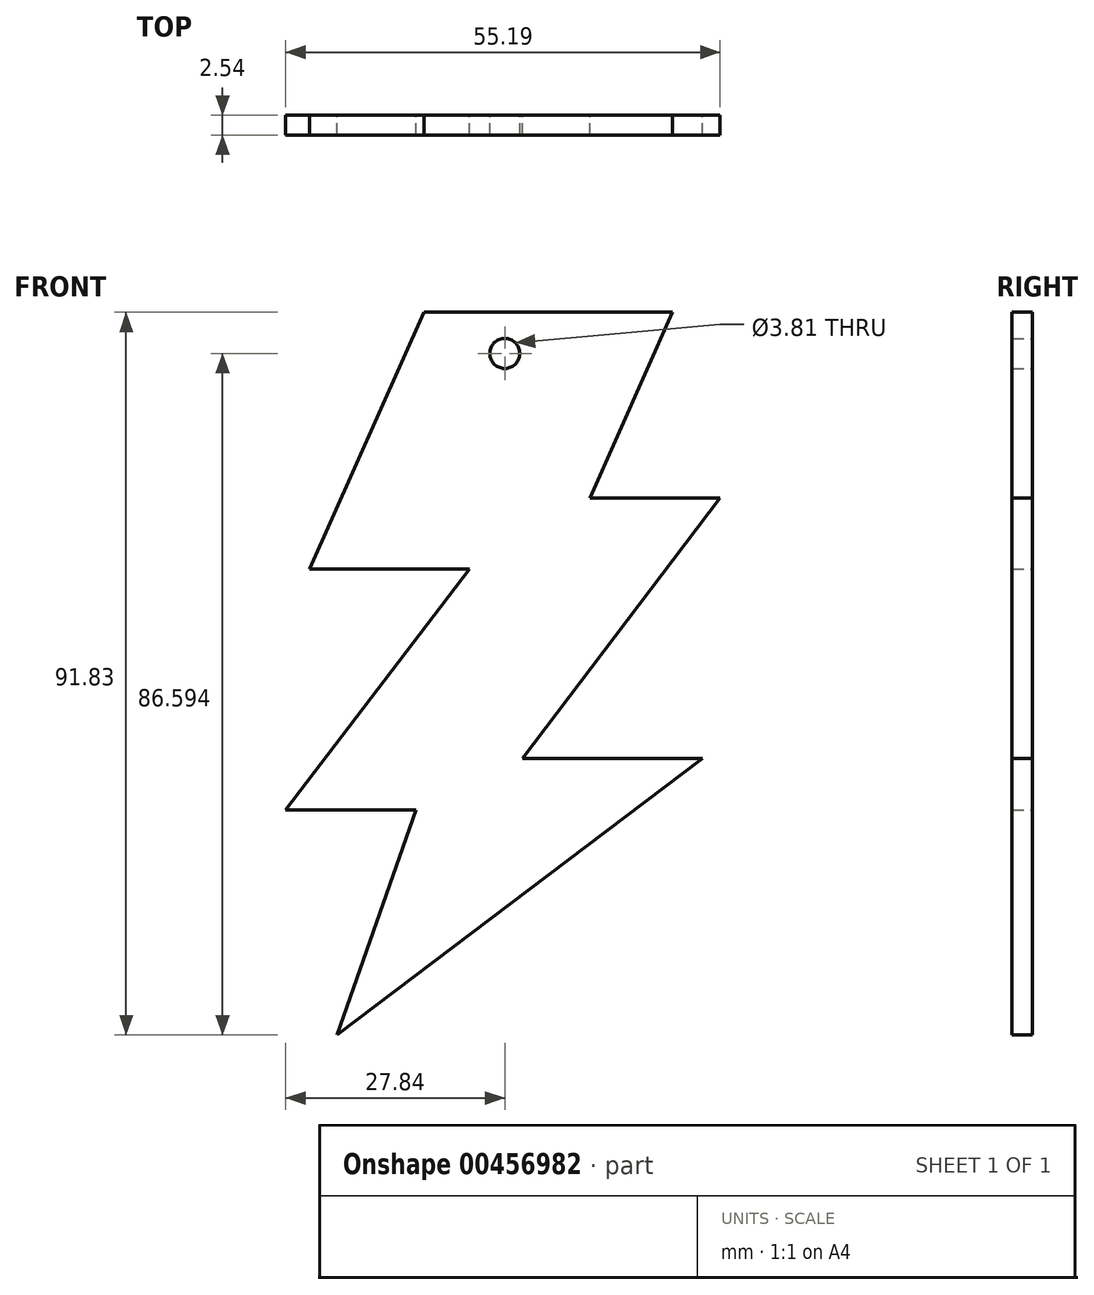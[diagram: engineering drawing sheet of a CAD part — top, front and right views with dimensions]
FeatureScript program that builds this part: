
annotation { "Feature Type Name" : "Feature", "Feature Type Description" : "" }
export const myFeature = defineFeature(function(context is Context, id is Id, definition is map)
    precondition{}
    {
        {
            var Q0;
            Q0=qCreatedBy(makeId("Front.planeOp"),FACE);
            var sketch = newSketch(context, id + "F0", { "sketchPlane" : qUnion([Q0])});
            skLineSegment(sketch, "E0", {"start": v(0, 76.78) * mm, "end": v(-31.6, 76.78) * mm});
            skLineSegment(sketch, "E1", {"start": v(-31.6, 76.78) * mm, "end": v(-46.16, 44.16) * mm});
            skLineSegment(sketch, "E2", {"start": v(-46.16, 44.16) * mm, "end": v(-25.84, 44.16) * mm});
            skLineSegment(sketch, "E3", {"start": v(-25.84, 44.16) * mm, "end": v(-49.17, 13.55) * mm});
            skLineSegment(sketch, "E4", {"start": v(-49.17, 13.55) * mm, "end": v(-32.62, 13.55) * mm});
            skLineSegment(sketch, "E5", {"start": v(0, 76.78) * mm, "end": v(-10.54, 53.19) * mm});
            skLineSegment(sketch, "E6", {"start": v(-10.54, 53.19) * mm, "end": v(6.02, 53.19) * mm});
            skLineSegment(sketch, "E7", {"start": v(6.02, 53.19) * mm, "end": v(-19.07, 20.07) * mm});
            skLineSegment(sketch, "E8", {"start": v(-19.07, 20.07) * mm, "end": v(3.76, 20.07) * mm});
            skLineSegment(sketch, "E9", {"start": v(3.76, 20.07) * mm, "end": v(-42.65, -15.05) * mm});
            skLineSegment(sketch, "E10", {"start": v(-42.65, -15.05) * mm, "end": v(-32.62, 13.55) * mm});
            skCircle(sketch, "E11", {"center": v(-21.33, 71.54) * mm, "radius": 1.9 * mm});
            skSolve(sketch);
        }
        {
            var Q0;
            Q0 = qSketchRegion(id + "F0", true);
            extrude(context, id + "F1", {"entities" : qUnion([Q0]), "depth" : 2.54 * mm});
        }
        {
            var Q0;
            Q0=makeQuery(id+"F0.imprint","IMPRINT",FACE,{"disambiguationData":[TD([[makeQuery(id+"F0.imprint","IMPRINT",EDGE,{"derivedFrom":sQuery(id+"F0.wireOp",EDGE,"E11")}),1.0]])]});
            extrude(context, id + "F2", {"entities" : qUnion([Q0]), "operationType" : NewBodyOperationType.REMOVE, "endBound" : BoundingType.THROUGH_ALL, "oppositeDirection" : true, "depth" : 2.54 * mm});
        }
    });
